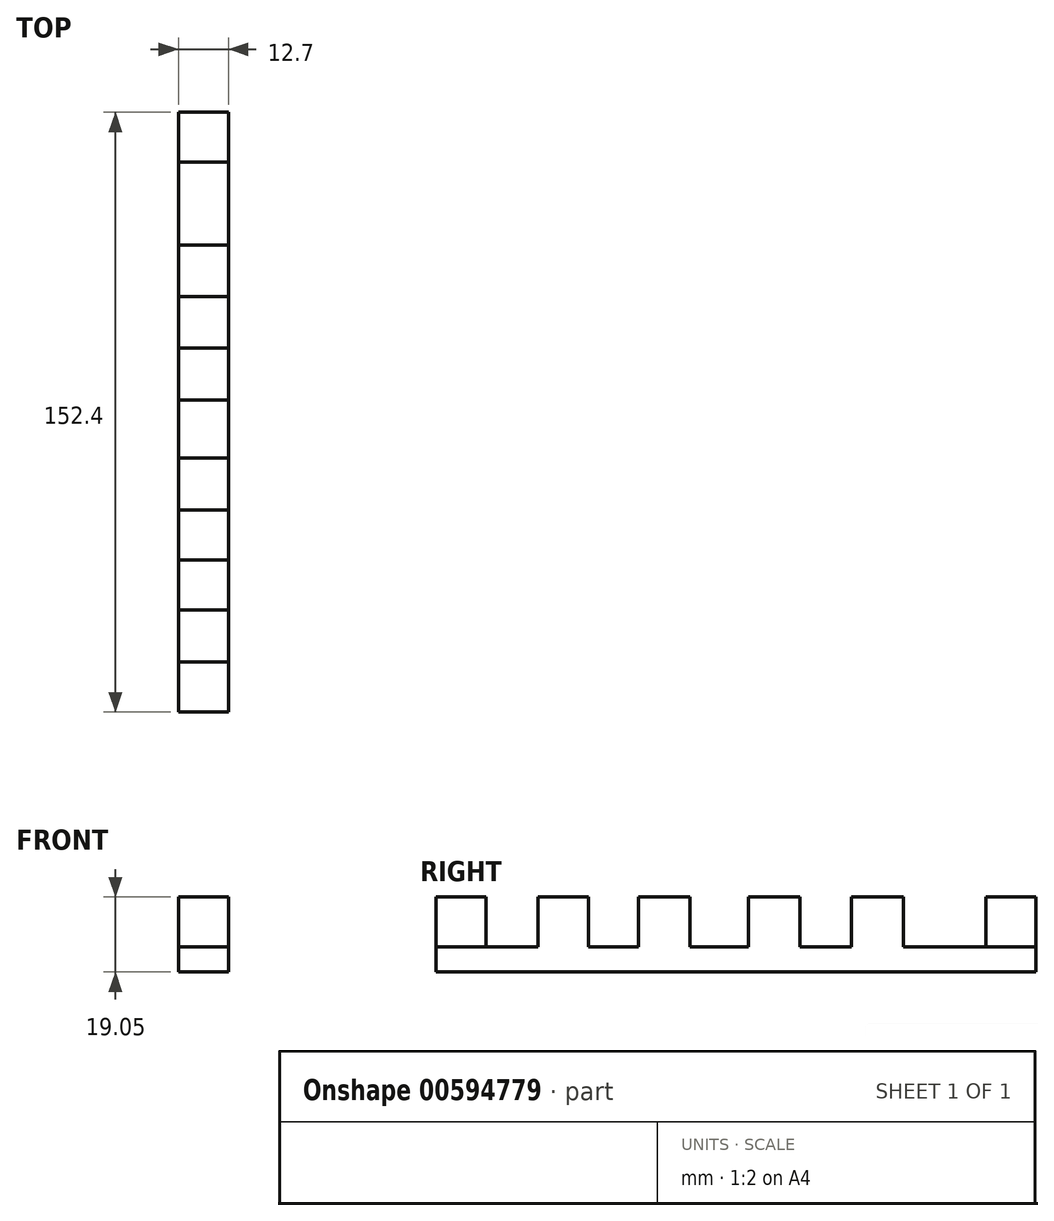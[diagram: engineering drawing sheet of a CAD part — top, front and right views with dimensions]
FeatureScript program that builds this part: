
annotation { "Feature Type Name" : "Feature", "Feature Type Description" : "" }
export const myFeature = defineFeature(function(context is Context, id is Id, definition is map)
    precondition{}
    {
        {
            var Q0;
            Q0=qCreatedBy(makeId("Top.planeOp"),FACE);
            var sketch = newSketch(context, id + "F0", { "sketchPlane" : qUnion([Q0])});
            skLineSegment(sketch, "E0.bottom", {"start": v(-77.5, 77.23) * mm, "end": v(-64.8, 77.23) * mm});
            skLineSegment(sketch, "E0.top", {"start": v(-77.5, -75.17) * mm, "end": v(-64.8, -75.17) * mm});
            skLineSegment(sketch, "E0.left", {"start": v(-77.5, 77.23) * mm, "end": v(-77.5, -75.17) * mm});
            skLineSegment(sketch, "E0.right", {"start": v(-64.8, 77.23) * mm, "end": v(-64.8, -75.17) * mm});
            skLineSegment(sketch, "E1.bottom", {"start": v(-57.47, 77.23) * mm, "end": v(-44.77, 77.23) * mm});
            skLineSegment(sketch, "E1.top", {"start": v(-57.47, -75.17) * mm, "end": v(-44.77, -75.17) * mm});
            skLineSegment(sketch, "E1.left", {"start": v(-57.47, 77.23) * mm, "end": v(-57.47, -75.17) * mm});
            skLineSegment(sketch, "E1.right", {"start": v(-44.77, 77.23) * mm, "end": v(-44.77, -75.17) * mm});
            skLineSegment(sketch, "E2.bottom", {"start": v(-39.1, 77.23) * mm, "end": v(-26.4, 77.23) * mm});
            skLineSegment(sketch, "E2.top", {"start": v(-39.1, -75.17) * mm, "end": v(-26.4, -75.17) * mm});
            skLineSegment(sketch, "E2.left", {"start": v(-39.1, 77.23) * mm, "end": v(-39.1, -75.17) * mm});
            skLineSegment(sketch, "E2.right", {"start": v(-26.4, 77.23) * mm, "end": v(-26.4, -75.17) * mm});
            skLineSegment(sketch, "E3.bottom", {"start": v(-22.82, 77.23) * mm, "end": v(-10.12, 77.23) * mm});
            skLineSegment(sketch, "E3.top", {"start": v(-22.82, -75.17) * mm, "end": v(-10.12, -75.17) * mm});
            skLineSegment(sketch, "E3.left", {"start": v(-22.82, 77.23) * mm, "end": v(-22.82, -75.17) * mm});
            skLineSegment(sketch, "E3.right", {"start": v(-10.12, 77.23) * mm, "end": v(-10.12, -75.17) * mm});
            skPoint(sketch, "E4.firstSnap0", {"position": v(-51.12, 77.23) * mm});
            skLineSegment(sketch, "E4.bottom", {"start": v(0, 77.23) * mm, "end": v(12.7, 77.23) * mm});
            skLineSegment(sketch, "E4.top", {"start": v(0, -75.17) * mm, "end": v(12.7, -75.17) * mm});
            skLineSegment(sketch, "E4.left", {"start": v(0, 77.23) * mm, "end": v(0, -75.17) * mm});
            skLineSegment(sketch, "E4.right", {"start": v(12.7, 77.23) * mm, "end": v(12.7, -75.17) * mm});
            skLineSegment(sketch, "E5.bottom", {"start": v(19.34, 77.23) * mm, "end": v(32.04, 77.23) * mm});
            skLineSegment(sketch, "E5.top", {"start": v(19.34, -75.17) * mm, "end": v(32.04, -75.17) * mm});
            skLineSegment(sketch, "E5.left", {"start": v(19.34, 77.23) * mm, "end": v(19.34, -75.17) * mm});
            skLineSegment(sketch, "E5.right", {"start": v(32.04, 77.23) * mm, "end": v(32.04, -75.17) * mm});
            skLineSegment(sketch, "E6.bottom", {"start": v(40.2, 77.23) * mm, "end": v(52.9, 77.23) * mm});
            skLineSegment(sketch, "E6.top", {"start": v(40.2, -75.17) * mm, "end": v(52.9, -75.17) * mm});
            skLineSegment(sketch, "E6.left", {"start": v(40.2, 77.23) * mm, "end": v(40.2, -75.17) * mm});
            skLineSegment(sketch, "E6.right", {"start": v(52.9, 77.23) * mm, "end": v(52.9, -75.17) * mm});
            skLineSegment(sketch, "E7.bottom", {"start": v(61.9, 77.23) * mm, "end": v(74.6, 77.23) * mm});
            skLineSegment(sketch, "E7.top", {"start": v(61.9, -75.17) * mm, "end": v(74.6, -75.17) * mm});
            skLineSegment(sketch, "E7.left", {"start": v(61.9, 77.23) * mm, "end": v(61.9, -75.17) * mm});
            skLineSegment(sketch, "E7.right", {"start": v(74.6, 77.23) * mm, "end": v(74.6, -75.17) * mm});
            skSolve(sketch);
        }
        {
            var Q0;
            Q0=makeQuery(id+"F0.imprint","IMPRINT",FACE,{"disambiguationData":[TD([[makeQuery(id+"F0.imprint","IMPRINT",EDGE,{"derivedFrom":sQuery(id+"F0.wireOp",EDGE,"E0.bottom")}),-1.0]])]});
            var Q1;
            Q1=makeQuery(id+"F0.imprint","IMPRINT",FACE,{"disambiguationData":[TD([[makeQuery(id+"F0.imprint","IMPRINT",EDGE,{"derivedFrom":sQuery(id+"F0.wireOp",EDGE,"E1.bottom")}),-1.0]])]});
            var Q2;
            Q2=makeQuery(id+"F0.imprint","IMPRINT",FACE,{"disambiguationData":[TD([[makeQuery(id+"F0.imprint","IMPRINT",EDGE,{"derivedFrom":sQuery(id+"F0.wireOp",EDGE,"E2.bottom")}),-1.0]])]});
            var Q3;
            Q3=makeQuery(id+"F0.imprint","IMPRINT",FACE,{"disambiguationData":[TD([[makeQuery(id+"F0.imprint","IMPRINT",EDGE,{"derivedFrom":sQuery(id+"F0.wireOp",EDGE,"E3.bottom")}),-1.0]])]});
            var Q4;
            Q4=makeQuery(id+"F0.imprint","IMPRINT",FACE,{"disambiguationData":[TD([[makeQuery(id+"F0.imprint","IMPRINT",EDGE,{"derivedFrom":sQuery(id+"F0.wireOp",EDGE,"E4.bottom")}),-1.0]])]});
            var Q5;
            Q5=makeQuery(id+"F0.imprint","IMPRINT",FACE,{"disambiguationData":[TD([[makeQuery(id+"F0.imprint","IMPRINT",EDGE,{"derivedFrom":sQuery(id+"F0.wireOp",EDGE,"E5.bottom")}),-1.0]])]});
            var Q6;
            Q6=makeQuery(id+"F0.imprint","IMPRINT",FACE,{"disambiguationData":[TD([[makeQuery(id+"F0.imprint","IMPRINT",EDGE,{"derivedFrom":sQuery(id+"F0.wireOp",EDGE,"E6.bottom")}),-1.0]])]});
            var Q7;
            Q7=makeQuery(id+"F0.imprint","IMPRINT",FACE,{"disambiguationData":[TD([[makeQuery(id+"F0.imprint","IMPRINT",EDGE,{"derivedFrom":sQuery(id+"F0.wireOp",EDGE,"E7.bottom")}),-1.0]])]});
            extrude(context, id + "F1", {"entities" : qUnion([Q0, Q1, Q2, Q3, Q4, Q5, Q6, Q7]), "depth" : 6.35 * mm, "offsetDistance" : 25.4 * mm});
        }
        {
            var Q0;
            Q0=makeQuery(id+"F1.opExtrude","CAP_FACE",FACE,{"disambiguationData":[OSD([sQuery(id+"F0.wireOp",EDGE,"E0.bottom"),sQuery(id+"F0.wireOp",EDGE,"E0.top"),sQuery(id+"F0.wireOp",EDGE,"E0.left"),sQuery(id+"F0.wireOp",EDGE,"E0.right")])],"isStart":false});
            var sketch = newSketch(context, id + "F2", { "sketchPlane" : qUnion([Q0])});
            skLineSegment(sketch, "E8.bottom", {"start": v(-77.5, 77.23) * mm, "end": v(-64.8, 77.23) * mm});
            skLineSegment(sketch, "E8.top", {"start": v(-77.5, 64.57) * mm, "end": v(-64.8, 64.57) * mm});
            skLineSegment(sketch, "E8.left", {"start": v(-77.5, 77.23) * mm, "end": v(-77.5, 64.57) * mm});
            skLineSegment(sketch, "E8.right", {"start": v(-64.8, 77.23) * mm, "end": v(-64.8, 64.57) * mm});
            skLineSegment(sketch, "E9.bottom", {"start": v(-57.25, 77.23) * mm, "end": v(-44.54, 77.23) * mm});
            skLineSegment(sketch, "E9.top", {"start": v(-57.25, 64.57) * mm, "end": v(-44.54, 64.57) * mm});
            skLineSegment(sketch, "E9.left", {"start": v(-57.25, 77.23) * mm, "end": v(-57.25, 64.57) * mm});
            skLineSegment(sketch, "E9.right", {"start": v(-44.54, 77.23) * mm, "end": v(-44.54, 64.57) * mm});
            skLineSegment(sketch, "E10.bottom", {"start": v(-38.89, 77.23) * mm, "end": v(-26.14, 77.23) * mm});
            skLineSegment(sketch, "E10.top", {"start": v(-38.89, 64.57) * mm, "end": v(-26.14, 64.57) * mm});
            skLineSegment(sketch, "E10.left", {"start": v(-38.89, 77.23) * mm, "end": v(-38.89, 64.57) * mm});
            skLineSegment(sketch, "E10.right", {"start": v(-26.14, 77.23) * mm, "end": v(-26.14, 64.57) * mm});
            skLineSegment(sketch, "E11.bottom", {"start": v(-22.4, 77.23) * mm, "end": v(-9.68, 77.23) * mm});
            skLineSegment(sketch, "E11.top", {"start": v(-22.4, 64.57) * mm, "end": v(-9.68, 64.57) * mm});
            skLineSegment(sketch, "E11.left", {"start": v(-22.4, 77.23) * mm, "end": v(-22.4, 64.57) * mm});
            skLineSegment(sketch, "E11.right", {"start": v(-9.68, 77.23) * mm, "end": v(-9.68, 64.57) * mm});
            skLineSegment(sketch, "E12.bottom", {"start": v(0, 77.23) * mm, "end": v(12.64, 77.23) * mm});
            skLineSegment(sketch, "E12.top", {"start": v(0, 64.57) * mm, "end": v(12.64, 64.57) * mm});
            skLineSegment(sketch, "E12.left", {"start": v(0, 77.23) * mm, "end": v(0, 64.57) * mm});
            skLineSegment(sketch, "E12.right", {"start": v(12.64, 77.23) * mm, "end": v(12.64, 64.57) * mm});
            skLineSegment(sketch, "E13.bottom", {"start": v(19.95, 77.23) * mm, "end": v(32.53, 77.23) * mm});
            skLineSegment(sketch, "E13.top", {"start": v(19.95, 64.57) * mm, "end": v(32.53, 64.57) * mm});
            skLineSegment(sketch, "E13.left", {"start": v(19.95, 77.23) * mm, "end": v(19.95, 64.57) * mm});
            skLineSegment(sketch, "E13.right", {"start": v(32.53, 77.23) * mm, "end": v(32.53, 64.57) * mm});
            skLineSegment(sketch, "E14.bottom", {"start": v(41.12, 77.23) * mm, "end": v(53.36, 77.23) * mm});
            skLineSegment(sketch, "E14.top", {"start": v(41.12, 64.57) * mm, "end": v(53.36, 64.57) * mm});
            skLineSegment(sketch, "E14.left", {"start": v(41.12, 77.23) * mm, "end": v(41.12, 64.57) * mm});
            skLineSegment(sketch, "E14.right", {"start": v(53.36, 77.23) * mm, "end": v(53.36, 64.57) * mm});
            skLineSegment(sketch, "E15.bottom", {"start": v(62.12, 77.23) * mm, "end": v(74.62, 77.23) * mm});
            skLineSegment(sketch, "E15.top", {"start": v(62.12, 64.57) * mm, "end": v(74.62, 64.57) * mm});
            skLineSegment(sketch, "E15.left", {"start": v(62.12, 77.23) * mm, "end": v(62.12, 64.57) * mm});
            skLineSegment(sketch, "E15.right", {"start": v(74.62, 77.23) * mm, "end": v(74.62, 64.57) * mm});
            skSolve(sketch);
        }
        {
            var Q0;
            Q0=makeQuery(id+"F2.imprint","IMPRINT",FACE,{"disambiguationData":[TD([[makeQuery(id+"F2.imprint","IMPRINT",EDGE,{"derivedFrom":sQuery(id+"F2.wireOp",EDGE,"E9.bottom")}),-1.0]])]});
            var Q1;
            Q1=makeQuery(id+"F2.imprint","IMPRINT",FACE,{"disambiguationData":[TD([[makeQuery(id+"F2.imprint","IMPRINT",EDGE,{"derivedFrom":sQuery(id+"F2.wireOp",EDGE,"E10.bottom")}),-1.0]])]});
            var Q2;
            Q2=makeQuery(id+"F2.imprint","IMPRINT",FACE,{"disambiguationData":[TD([[makeQuery(id+"F2.imprint","IMPRINT",EDGE,{"derivedFrom":sQuery(id+"F2.wireOp",EDGE,"E11.bottom")}),-1.0]])]});
            var Q3;
            Q3=makeQuery(id+"F2.imprint","IMPRINT",FACE,{"disambiguationData":[TD([[makeQuery(id+"F2.imprint","IMPRINT",EDGE,{"derivedFrom":sQuery(id+"F2.wireOp",EDGE,"E12.bottom")}),-1.0]])]});
            var Q4;
            Q4=makeQuery(id+"F2.imprint","IMPRINT",FACE,{"disambiguationData":[TD([[makeQuery(id+"F2.imprint","IMPRINT",EDGE,{"derivedFrom":sQuery(id+"F2.wireOp",EDGE,"E13.bottom")}),-1.0]])]});
            var Q5;
            Q5=makeQuery(id+"F2.imprint","IMPRINT",FACE,{"disambiguationData":[TD([[makeQuery(id+"F2.imprint","IMPRINT",EDGE,{"derivedFrom":sQuery(id+"F2.wireOp",EDGE,"E14.bottom")}),-1.0]])]});
            var Q6;
            Q6=makeQuery(id+"F2.imprint","IMPRINT",FACE,{"disambiguationData":[TD([[makeQuery(id+"F2.imprint","IMPRINT",EDGE,{"derivedFrom":sQuery(id+"F2.wireOp",EDGE,"E15.bottom")}),-1.0]])]});
            var Q7;
            Q7=makeQuery(id+"F2.imprint","IMPRINT",FACE,{"disambiguationData":[TD([[makeQuery(id+"F2.imprint","IMPRINT",EDGE,{"derivedFrom":sQuery(id+"F2.wireOp",EDGE,"E8.bottom")}),-1.0]])]});
            extrude(context, id + "F3", {"entities" : qUnion([Q0, Q1, Q2, Q3, Q4, Q5, Q6, Q7]), "depth" : 12.7 * mm, "offsetDistance" : 25.4 * mm});
        }
        {
            var Q0;
            Q0=makeQuery(id+"F1.opExtrude","CAP_FACE",FACE,{"disambiguationData":[OSD([sQuery(id+"F0.wireOp",EDGE,"E0.bottom"),sQuery(id+"F0.wireOp",EDGE,"E0.top"),sQuery(id+"F0.wireOp",EDGE,"E0.left"),sQuery(id+"F0.wireOp",EDGE,"E0.right")])],"isStart":false});
            var sketch = newSketch(context, id + "F4", { "sketchPlane" : qUnion([Q0])});
            skLineSegment(sketch, "E16.bottom", {"start": v(-77.5, -75.17) * mm, "end": v(-64.8, -75.17) * mm});
            skLineSegment(sketch, "E16.top", {"start": v(-77.5, -62.48) * mm, "end": v(-64.8, -62.48) * mm});
            skLineSegment(sketch, "E16.left", {"start": v(-77.5, -75.17) * mm, "end": v(-77.5, -62.48) * mm});
            skLineSegment(sketch, "E16.right", {"start": v(-64.8, -75.17) * mm, "end": v(-64.8, -62.48) * mm});
            skLineSegment(sketch, "E17.bottom", {"start": v(-57.62, -75.17) * mm, "end": v(-45.3, -75.17) * mm});
            skLineSegment(sketch, "E17.top", {"start": v(-57.62, -62.48) * mm, "end": v(-45.3, -62.48) * mm});
            skLineSegment(sketch, "E17.left", {"start": v(-57.62, -75.17) * mm, "end": v(-57.62, -62.48) * mm});
            skLineSegment(sketch, "E17.right", {"start": v(-45.3, -75.17) * mm, "end": v(-45.3, -62.48) * mm});
            skLineSegment(sketch, "E18.bottom", {"start": v(-39.24, -75.17) * mm, "end": v(-26.27, -75.17) * mm});
            skLineSegment(sketch, "E18.top", {"start": v(-39.24, -62.48) * mm, "end": v(-26.27, -62.48) * mm});
            skLineSegment(sketch, "E18.left", {"start": v(-39.24, -75.17) * mm, "end": v(-39.24, -62.48) * mm});
            skLineSegment(sketch, "E18.right", {"start": v(-26.27, -75.17) * mm, "end": v(-26.27, -62.48) * mm});
            skLineSegment(sketch, "E19.bottom", {"start": v(-22.74, -75.17) * mm, "end": v(-10.04, -75.17) * mm});
            skLineSegment(sketch, "E19.top", {"start": v(-22.74, -62.48) * mm, "end": v(-10.04, -62.48) * mm});
            skLineSegment(sketch, "E19.left", {"start": v(-22.74, -75.17) * mm, "end": v(-22.74, -62.48) * mm});
            skLineSegment(sketch, "E19.right", {"start": v(-10.04, -75.17) * mm, "end": v(-10.04, -62.48) * mm});
            skLineSegment(sketch, "E20.bottom", {"start": v(0, -75.17) * mm, "end": v(12.85, -75.17) * mm});
            skLineSegment(sketch, "E20.top", {"start": v(0, -62.48) * mm, "end": v(12.85, -62.48) * mm});
            skLineSegment(sketch, "E20.left", {"start": v(0, -75.17) * mm, "end": v(0, -62.48) * mm});
            skLineSegment(sketch, "E20.right", {"start": v(12.85, -75.17) * mm, "end": v(12.85, -62.48) * mm});
            skLineSegment(sketch, "E21.bottom", {"start": v(19.07, -75.17) * mm, "end": v(32.22, -75.17) * mm});
            skLineSegment(sketch, "E21.top", {"start": v(19.07, -62.48) * mm, "end": v(32.22, -62.48) * mm});
            skLineSegment(sketch, "E21.left", {"start": v(19.07, -75.17) * mm, "end": v(19.07, -62.48) * mm});
            skLineSegment(sketch, "E21.right", {"start": v(32.22, -75.17) * mm, "end": v(32.22, -62.48) * mm});
            skLineSegment(sketch, "E22.bottom", {"start": v(40.05, -75.17) * mm, "end": v(52.58, -75.17) * mm});
            skLineSegment(sketch, "E22.top", {"start": v(40.05, -62.48) * mm, "end": v(52.58, -62.48) * mm});
            skLineSegment(sketch, "E22.left", {"start": v(40.05, -75.17) * mm, "end": v(40.05, -62.48) * mm});
            skLineSegment(sketch, "E22.right", {"start": v(52.58, -75.17) * mm, "end": v(52.58, -62.48) * mm});
            skLineSegment(sketch, "E23.bottom", {"start": v(62.38, -75.17) * mm, "end": v(74.35, -75.17) * mm});
            skLineSegment(sketch, "E23.top", {"start": v(62.38, -62.48) * mm, "end": v(74.35, -62.48) * mm});
            skLineSegment(sketch, "E23.left", {"start": v(62.38, -75.17) * mm, "end": v(62.38, -62.48) * mm});
            skLineSegment(sketch, "E23.right", {"start": v(74.35, -75.17) * mm, "end": v(74.35, -62.48) * mm});
            skSolve(sketch);
        }
        {
            var Q0;
            Q0=makeQuery(id+"F4.imprint","IMPRINT",FACE,{"disambiguationData":[TD([[makeQuery(id+"F4.imprint","IMPRINT",EDGE,{"derivedFrom":sQuery(id+"F4.wireOp",EDGE,"E17.bottom")}),1.0]])]});
            var Q1;
            Q1=makeQuery(id+"F4.imprint","IMPRINT",FACE,{"disambiguationData":[TD([[makeQuery(id+"F4.imprint","IMPRINT",EDGE,{"derivedFrom":sQuery(id+"F4.wireOp",EDGE,"E18.bottom")}),1.0]])]});
            var Q2;
            Q2=makeQuery(id+"F4.imprint","IMPRINT",FACE,{"disambiguationData":[TD([[makeQuery(id+"F4.imprint","IMPRINT",EDGE,{"derivedFrom":sQuery(id+"F4.wireOp",EDGE,"E19.bottom")}),1.0]])]});
            var Q3;
            Q3=makeQuery(id+"F4.imprint","IMPRINT",FACE,{"disambiguationData":[TD([[makeQuery(id+"F4.imprint","IMPRINT",EDGE,{"derivedFrom":sQuery(id+"F4.wireOp",EDGE,"E20.bottom")}),1.0]])]});
            var Q4;
            Q4=makeQuery(id+"F4.imprint","IMPRINT",FACE,{"disambiguationData":[TD([[makeQuery(id+"F4.imprint","IMPRINT",EDGE,{"derivedFrom":sQuery(id+"F4.wireOp",EDGE,"E21.bottom")}),1.0]])]});
            var Q5;
            Q5=makeQuery(id+"F4.imprint","IMPRINT",FACE,{"disambiguationData":[TD([[makeQuery(id+"F4.imprint","IMPRINT",EDGE,{"derivedFrom":sQuery(id+"F4.wireOp",EDGE,"E22.bottom")}),1.0]])]});
            var Q6;
            Q6=makeQuery(id+"F4.imprint","IMPRINT",FACE,{"disambiguationData":[TD([[makeQuery(id+"F4.imprint","IMPRINT",EDGE,{"derivedFrom":sQuery(id+"F4.wireOp",EDGE,"E23.bottom")}),1.0]])]});
            var Q7;
            Q7=makeQuery(id+"F4.imprint","IMPRINT",FACE,{"disambiguationData":[TD([[makeQuery(id+"F4.imprint","IMPRINT",EDGE,{"derivedFrom":sQuery(id+"F4.wireOp",EDGE,"E16.bottom")}),1.0]])]});
            extrude(context, id + "F5", {"entities" : qUnion([Q0, Q1, Q2, Q3, Q4, Q5, Q6, Q7]), "depth" : 12.7 * mm, "offsetDistance" : 25.4 * mm});
        }
        {
            var Q0;
            Q0=makeQuery(id+"F1.opExtrude","CAP_FACE",FACE,{"disambiguationData":[OSD([sQuery(id+"F0.wireOp",EDGE,"E0.bottom"),sQuery(id+"F0.wireOp",EDGE,"E0.top"),sQuery(id+"F0.wireOp",EDGE,"E0.left"),sQuery(id+"F0.wireOp",EDGE,"E0.right")])],"isStart":false});
            var sketch = newSketch(context, id + "F6", { "sketchPlane" : qUnion([Q0])});
            skLineSegment(sketch, "E24.bottom", {"start": v(-77.5, -61.91) * mm, "end": v(-64.8, -61.91) * mm});
            skLineSegment(sketch, "E24.top", {"start": v(-77.5, -49.22) * mm, "end": v(-64.8, -49.22) * mm});
            skLineSegment(sketch, "E24.left", {"start": v(-77.5, -61.91) * mm, "end": v(-77.5, -49.22) * mm});
            skLineSegment(sketch, "E24.right", {"start": v(-64.8, -61.91) * mm, "end": v(-64.8, -49.22) * mm});
            skLineSegment(sketch, "E25.top", {"start": v(-77.5, -36.5) * mm, "end": v(-64.8, -36.5) * mm});
            skLineSegment(sketch, "E25.left", {"start": v(-77.5, -49.22) * mm, "end": v(-77.5, -36.5) * mm});
            skLineSegment(sketch, "E25.right", {"start": v(-64.8, -49.22) * mm, "end": v(-64.8, -36.5) * mm});
            skLineSegment(sketch, "E26.top", {"start": v(-77.5, -23.77) * mm, "end": v(-64.8, -23.77) * mm});
            skLineSegment(sketch, "E26.left", {"start": v(-77.5, -36.5) * mm, "end": v(-77.5, -23.77) * mm});
            skLineSegment(sketch, "E26.right", {"start": v(-64.8, -36.5) * mm, "end": v(-64.8, -23.77) * mm});
            skLineSegment(sketch, "E27.top", {"start": v(-77.5, -10.67) * mm, "end": v(-64.8, -10.67) * mm});
            skLineSegment(sketch, "E27.left", {"start": v(-77.5, -23.77) * mm, "end": v(-77.5, -10.67) * mm});
            skLineSegment(sketch, "E27.right", {"start": v(-64.8, -23.77) * mm, "end": v(-64.8, -10.67) * mm});
            skLineSegment(sketch, "E28.top", {"start": v(-77.5, 4.15) * mm, "end": v(-64.8, 4.15) * mm});
            skLineSegment(sketch, "E28.left", {"start": v(-77.5, -10.67) * mm, "end": v(-77.5, 4.15) * mm});
            skLineSegment(sketch, "E28.right", {"start": v(-64.8, -10.67) * mm, "end": v(-64.8, 4.15) * mm});
            skLineSegment(sketch, "E29.top", {"start": v(-77.5, 17.3) * mm, "end": v(-64.8, 17.3) * mm});
            skLineSegment(sketch, "E29.left", {"start": v(-77.5, 4.15) * mm, "end": v(-77.5, 17.3) * mm});
            skLineSegment(sketch, "E29.right", {"start": v(-64.8, 4.15) * mm, "end": v(-64.8, 17.3) * mm});
            skLineSegment(sketch, "E30.top", {"start": v(-77.5, 30.36) * mm, "end": v(-64.8, 30.36) * mm});
            skLineSegment(sketch, "E30.left", {"start": v(-77.5, 17.3) * mm, "end": v(-77.5, 30.36) * mm});
            skLineSegment(sketch, "E30.right", {"start": v(-64.8, 17.3) * mm, "end": v(-64.8, 30.36) * mm});
            skLineSegment(sketch, "E31.top", {"start": v(-77.5, 43.52) * mm, "end": v(-64.8, 43.52) * mm});
            skLineSegment(sketch, "E31.left", {"start": v(-77.5, 30.36) * mm, "end": v(-77.5, 43.52) * mm});
            skLineSegment(sketch, "E31.right", {"start": v(-64.8, 30.36) * mm, "end": v(-64.8, 43.52) * mm});
            skLineSegment(sketch, "E32.top", {"start": v(-77.5, 64.58) * mm, "end": v(-64.8, 64.58) * mm});
            skLineSegment(sketch, "E32.left", {"start": v(-77.5, 43.52) * mm, "end": v(-77.5, 64.58) * mm});
            skLineSegment(sketch, "E32.right", {"start": v(-64.8, 43.52) * mm, "end": v(-64.8, 64.58) * mm});
            skSolve(sketch);
        }
        {
            var Q0;
            Q0=makeQuery(id+"F6.imprint","IMPRINT",FACE,{"disambiguationData":[TD([[makeQuery(id+"F6.imprint","IMPRINT",EDGE,{"derivedFrom":sQuery(id+"F6.wireOp",EDGE,"E26.top")}),1.0]])]});
            var Q1;
            Q1=makeQuery(id+"F6.imprint","IMPRINT",FACE,{"disambiguationData":[TD([[makeQuery(id+"F6.imprint","IMPRINT",EDGE,{"derivedFrom":sQuery(id+"F6.wireOp",EDGE,"E28.top")}),1.0]])]});
            var Q2;
            Q2=makeQuery(id+"F6.imprint","IMPRINT",FACE,{"disambiguationData":[TD([[makeQuery(id+"F6.imprint","IMPRINT",EDGE,{"derivedFrom":sQuery(id+"F6.wireOp",EDGE,"E30.top")}),1.0]])]});
            var Q3;
            Q3=makeQuery(id+"F6.imprint","IMPRINT",FACE,{"disambiguationData":[TD([[makeQuery(id+"F6.imprint","IMPRINT",EDGE,{"derivedFrom":sQuery(id+"F6.wireOp",EDGE,"E24.top")}),1.0]])]});
            extrude(context, id + "F7", {"entities" : qUnion([Q0, Q1, Q2, Q3]), "operationType" : NewBodyOperationType.ADD, "depth" : 12.7 * mm, "offsetDistance" : 25.4 * mm});
        }
        {
            var Q0;
            Q0=makeQuery(id+"F1.opExtrude","SWEPT_BODY",BODY,{"disambiguationData":[OSD([sQuery(id+"F0.wireOp",EDGE,"E1.bottom"),sQuery(id+"F0.wireOp",EDGE,"E1.top"),sQuery(id+"F0.wireOp",EDGE,"E1.left"),sQuery(id+"F0.wireOp",EDGE,"E1.right")])]});
            var Q1;
            Q1=makeQuery(id+"F1.opExtrude","SWEPT_BODY",BODY,{"disambiguationData":[OSD([sQuery(id+"F0.wireOp",EDGE,"E2.bottom"),sQuery(id+"F0.wireOp",EDGE,"E2.top"),sQuery(id+"F0.wireOp",EDGE,"E2.left"),sQuery(id+"F0.wireOp",EDGE,"E2.right")])]});
            var Q2;
            Q2=makeQuery(id+"F1.opExtrude","SWEPT_BODY",BODY,{"disambiguationData":[OSD([sQuery(id+"F0.wireOp",EDGE,"E3.bottom"),sQuery(id+"F0.wireOp",EDGE,"E3.top"),sQuery(id+"F0.wireOp",EDGE,"E3.left"),sQuery(id+"F0.wireOp",EDGE,"E3.right")])]});
            var Q3;
            Q3=makeQuery(id+"F1.opExtrude","SWEPT_BODY",BODY,{"disambiguationData":[OSD([sQuery(id+"F0.wireOp",EDGE,"E4.bottom"),sQuery(id+"F0.wireOp",EDGE,"E4.top"),sQuery(id+"F0.wireOp",EDGE,"E4.left"),sQuery(id+"F0.wireOp",EDGE,"E4.right")])]});
            var Q4;
            Q4=makeQuery(id+"F1.opExtrude","SWEPT_BODY",BODY,{"disambiguationData":[OSD([sQuery(id+"F0.wireOp",EDGE,"E5.bottom"),sQuery(id+"F0.wireOp",EDGE,"E5.top"),sQuery(id+"F0.wireOp",EDGE,"E5.left"),sQuery(id+"F0.wireOp",EDGE,"E5.right")])]});
            var Q5;
            Q5=makeQuery(id+"F1.opExtrude","SWEPT_BODY",BODY,{"disambiguationData":[OSD([sQuery(id+"F0.wireOp",EDGE,"E6.bottom"),sQuery(id+"F0.wireOp",EDGE,"E6.top"),sQuery(id+"F0.wireOp",EDGE,"E6.left"),sQuery(id+"F0.wireOp",EDGE,"E6.right")])]});
            var Q6;
            Q6=makeQuery(id+"F1.opExtrude","SWEPT_BODY",BODY,{"disambiguationData":[OSD([sQuery(id+"F0.wireOp",EDGE,"E7.bottom"),sQuery(id+"F0.wireOp",EDGE,"E7.top"),sQuery(id+"F0.wireOp",EDGE,"E7.left"),sQuery(id+"F0.wireOp",EDGE,"E7.right")])]});
            var Q7;
            Q7=makeQuery(id+"F5.opExtrude","SWEPT_BODY",BODY,{"disambiguationData":[OSD([sQuery(id+"F4.wireOp",EDGE,"E17.bottom"),sQuery(id+"F4.wireOp",EDGE,"E17.top"),sQuery(id+"F4.wireOp",EDGE,"E17.left"),sQuery(id+"F4.wireOp",EDGE,"E17.right")])]});
            var Q8;
            Q8=makeQuery(id+"F5.opExtrude","SWEPT_BODY",BODY,{"disambiguationData":[OSD([sQuery(id+"F4.wireOp",EDGE,"E18.bottom"),sQuery(id+"F4.wireOp",EDGE,"E18.top"),sQuery(id+"F4.wireOp",EDGE,"E18.left"),sQuery(id+"F4.wireOp",EDGE,"E18.right")])]});
            var Q9;
            Q9=makeQuery(id+"F5.opExtrude","SWEPT_BODY",BODY,{"disambiguationData":[OSD([sQuery(id+"F4.wireOp",EDGE,"E19.bottom"),sQuery(id+"F4.wireOp",EDGE,"E19.top"),sQuery(id+"F4.wireOp",EDGE,"E19.left"),sQuery(id+"F4.wireOp",EDGE,"E19.right")])]});
            var Q10;
            Q10=makeQuery(id+"F5.opExtrude","SWEPT_BODY",BODY,{"disambiguationData":[OSD([sQuery(id+"F4.wireOp",EDGE,"E20.bottom"),sQuery(id+"F4.wireOp",EDGE,"E20.top"),sQuery(id+"F4.wireOp",EDGE,"E20.left"),sQuery(id+"F4.wireOp",EDGE,"E20.right")])]});
            var Q11;
            Q11=makeQuery(id+"F5.opExtrude","SWEPT_BODY",BODY,{"disambiguationData":[OSD([sQuery(id+"F4.wireOp",EDGE,"E21.bottom"),sQuery(id+"F4.wireOp",EDGE,"E21.top"),sQuery(id+"F4.wireOp",EDGE,"E21.left"),sQuery(id+"F4.wireOp",EDGE,"E21.right")])]});
            var Q12;
            Q12=makeQuery(id+"F5.opExtrude","SWEPT_BODY",BODY,{"disambiguationData":[OSD([sQuery(id+"F4.wireOp",EDGE,"E22.bottom"),sQuery(id+"F4.wireOp",EDGE,"E22.top"),sQuery(id+"F4.wireOp",EDGE,"E22.left"),sQuery(id+"F4.wireOp",EDGE,"E22.right")])]});
            var Q13;
            Q13=makeQuery(id+"F5.opExtrude","SWEPT_BODY",BODY,{"disambiguationData":[OSD([sQuery(id+"F4.wireOp",EDGE,"E23.bottom"),sQuery(id+"F4.wireOp",EDGE,"E23.top"),sQuery(id+"F4.wireOp",EDGE,"E23.left"),sQuery(id+"F4.wireOp",EDGE,"E23.right")])]});
            var Q14;
            Q14=makeQuery(id+"F3.opExtrude","SWEPT_BODY",BODY,{"disambiguationData":[OSD([sQuery(id+"F2.wireOp",EDGE,"E15.bottom"),sQuery(id+"F2.wireOp",EDGE,"E15.top"),sQuery(id+"F2.wireOp",EDGE,"E15.left"),sQuery(id+"F2.wireOp",EDGE,"E15.right")])]});
            var Q15;
            Q15=makeQuery(id+"F3.opExtrude","SWEPT_BODY",BODY,{"disambiguationData":[OSD([sQuery(id+"F2.wireOp",EDGE,"E14.bottom"),sQuery(id+"F2.wireOp",EDGE,"E14.top"),sQuery(id+"F2.wireOp",EDGE,"E14.left"),sQuery(id+"F2.wireOp",EDGE,"E14.right")])]});
            var Q16;
            Q16=makeQuery(id+"F3.opExtrude","SWEPT_BODY",BODY,{"disambiguationData":[OSD([sQuery(id+"F2.wireOp",EDGE,"E13.bottom"),sQuery(id+"F2.wireOp",EDGE,"E13.top"),sQuery(id+"F2.wireOp",EDGE,"E13.left"),sQuery(id+"F2.wireOp",EDGE,"E13.right")])]});
            var Q17;
            Q17=makeQuery(id+"F3.opExtrude","SWEPT_BODY",BODY,{"disambiguationData":[OSD([sQuery(id+"F2.wireOp",EDGE,"E12.bottom"),sQuery(id+"F2.wireOp",EDGE,"E12.top"),sQuery(id+"F2.wireOp",EDGE,"E12.left"),sQuery(id+"F2.wireOp",EDGE,"E12.right")])]});
            var Q18;
            Q18=makeQuery(id+"F3.opExtrude","SWEPT_BODY",BODY,{"disambiguationData":[OSD([sQuery(id+"F2.wireOp",EDGE,"E11.bottom"),sQuery(id+"F2.wireOp",EDGE,"E11.top"),sQuery(id+"F2.wireOp",EDGE,"E11.left"),sQuery(id+"F2.wireOp",EDGE,"E11.right")])]});
            var Q19;
            Q19=makeQuery(id+"F3.opExtrude","SWEPT_BODY",BODY,{"disambiguationData":[OSD([sQuery(id+"F2.wireOp",EDGE,"E10.bottom"),sQuery(id+"F2.wireOp",EDGE,"E10.top"),sQuery(id+"F2.wireOp",EDGE,"E10.left"),sQuery(id+"F2.wireOp",EDGE,"E10.right")])]});
            var Q20;
            Q20=makeQuery(id+"F3.opExtrude","SWEPT_BODY",BODY,{"disambiguationData":[OSD([sQuery(id+"F2.wireOp",EDGE,"E9.bottom"),sQuery(id+"F2.wireOp",EDGE,"E9.top"),sQuery(id+"F2.wireOp",EDGE,"E9.left"),sQuery(id+"F2.wireOp",EDGE,"E9.right")])]});
            deleteBodies(context, id + "F8", {"entities" : qUnion([Q0, Q1, Q2, Q3, Q4, Q5, Q6, Q7, Q8, Q9, Q10, Q11, Q12, Q13, Q14, Q15, Q16, Q17, Q18, Q19, Q20])});
        }
    });
